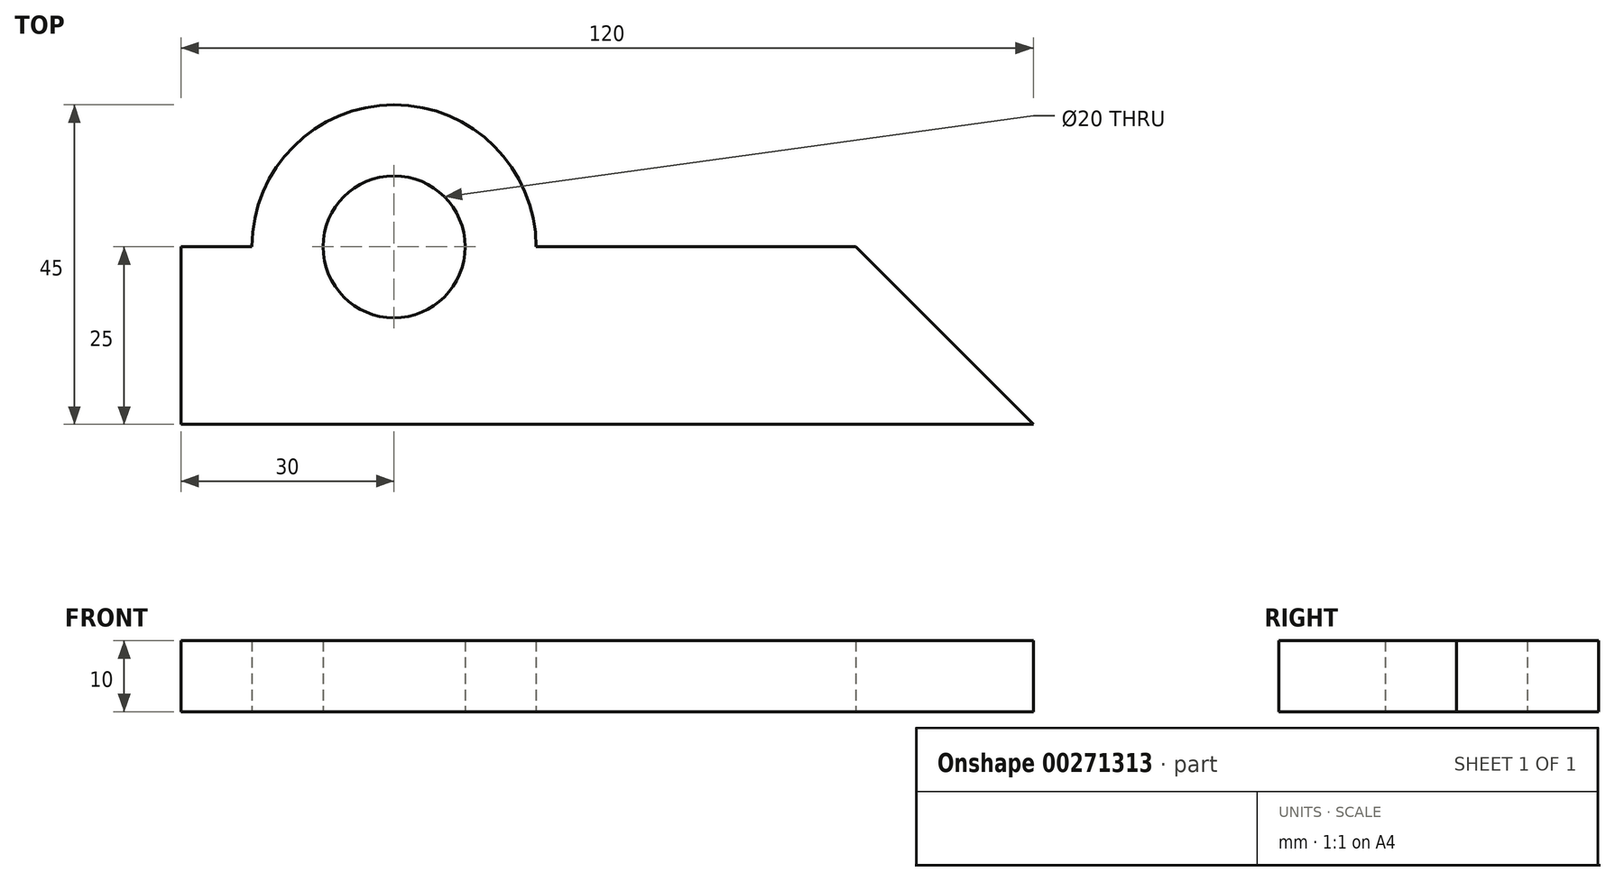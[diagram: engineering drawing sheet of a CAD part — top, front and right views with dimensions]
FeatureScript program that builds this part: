
annotation { "Feature Type Name" : "Feature", "Feature Type Description" : "" }
export const myFeature = defineFeature(function(context is Context, id is Id, definition is map)
    precondition{}
    {
        {
            var Q0;
            Q0=qCreatedBy(makeId("Top.planeOp"),FACE);
            var sketch = newSketch(context, id + "F0", { "sketchPlane" : qUnion([Q0])});
            skLineSegment(sketch, "E0.bottom", {"start": v(0, 0) * mm, "end": v(120, 0) * mm});
            skLineSegment(sketch, "E0.top", {"start": v(0, 25) * mm, "end": v(10, 25) * mm});
            skLineSegment(sketch, "E0.left", {"start": v(0, 0) * mm, "end": v(0, 25) * mm});
            skPoint(sketch, "E1", {"position": v(30, 25) * mm});
            skCircle(sketch, "E2", {"center": v(30, 25) * mm, "radius": 10 * mm});
            skArc(sketch, "E3", {"start": v(50, 25) * mm, "mid": v(30, 45) * mm, "end": v(10, 25) * mm});
            skLineSegment(sketch, "E4", {"start": v(120, 0) * mm, "end": v(95, 25) * mm});
            skLineSegment(sketch, "E5.trimOffspring", {"start": v(20, 25) * mm, "end": v(40, 25) * mm});
            skLineSegment(sketch, "E6.trimOffspring", {"start": v(50, 25) * mm, "end": v(95, 25) * mm});
            skSolve(sketch);
        }
        {
            var Q0;
            Q0 = qSketchRegion(id + "F0", true);
            extrude(context, id + "F1", {"entities" : qUnion([Q0]), "depth" : 10 * mm});
        }
    });
